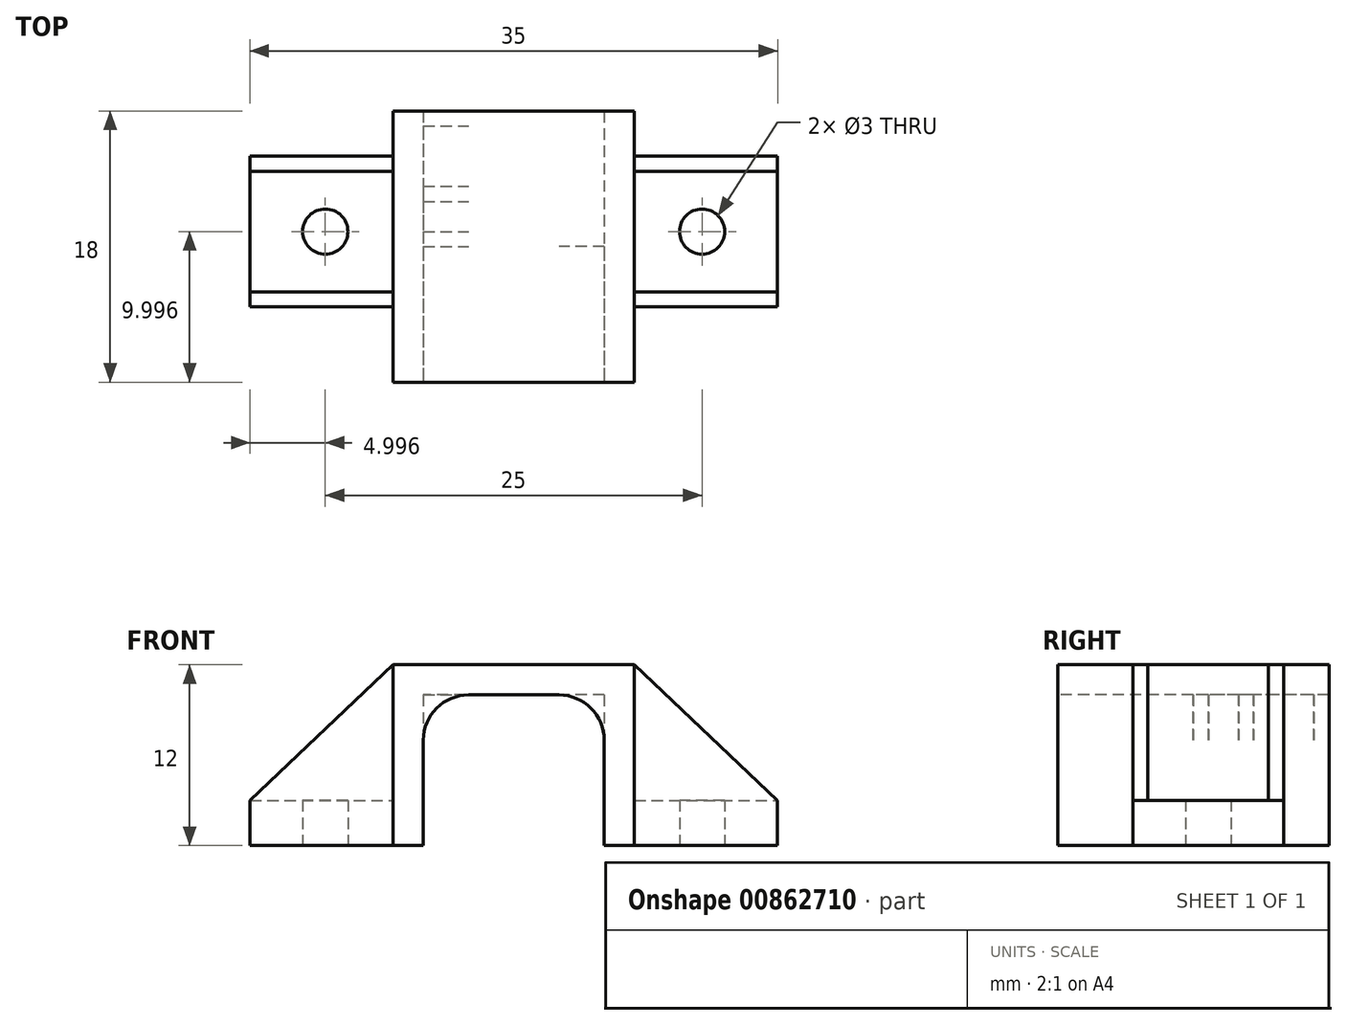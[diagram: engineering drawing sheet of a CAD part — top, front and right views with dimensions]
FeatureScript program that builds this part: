
annotation { "Feature Type Name" : "Feature", "Feature Type Description" : "" }
export const myFeature = defineFeature(function(context is Context, id is Id, definition is map)
    precondition{}
    {
        {
            var Q0;
            Q0=qCreatedBy(makeId("Top.planeOp"),FACE);
            var sketch = newSketch(context, id + "F0", { "sketchPlane" : qUnion([Q0])});
            skLineSegment(sketch, "E0.bottom", {"start": v(-19.82, -6.68) * mm, "end": v(15.18, -6.68) * mm});
            skLineSegment(sketch, "E0.top", {"start": v(-19.82, 3.32) * mm, "end": v(15.18, 3.32) * mm});
            skLineSegment(sketch, "E0.left", {"start": v(-19.82, -6.68) * mm, "end": v(-19.82, 3.32) * mm});
            skLineSegment(sketch, "E0.right", {"start": v(15.18, -6.68) * mm, "end": v(15.18, 3.32) * mm});
            skCircle(sketch, "E1", {"center": v(-14.82, -1.68) * mm, "radius": 1.5 * mm});
            skCircle(sketch, "E2", {"center": v(10.18, -1.68) * mm, "radius": 1.5 * mm});
            skLineSegment(sketch, "E3.bottom", {"start": v(-10.32, 6.32) * mm, "end": v(5.68, 6.32) * mm});
            skLineSegment(sketch, "E3.top", {"start": v(-10.32, -11.68) * mm, "end": v(5.68, -11.68) * mm});
            skLineSegment(sketch, "E3.left", {"start": v(-10.32, 6.32) * mm, "end": v(-10.32, -11.68) * mm});
            skLineSegment(sketch, "E3.right", {"start": v(5.68, 6.32) * mm, "end": v(5.68, -11.68) * mm});
            skSolve(sketch);
        }
        {
            var Q0;
            {var subQ5=sQuery(id+"F0.wireOp",EDGE,"E3.bottom");Q0=makeQuery(id+"F0.imprint","IMPRINT",FACE,{"disambiguationData":[TD([[makeQuery(id+"F0.imprint","IMPRINT",EDGE,{"derivedFrom":subQ5}),-1.0]])]});}
            var Q1;
            {var subQ0=sQuery(id+"F0.wireOp",EDGE,"E3.left");var subQ1=sQuery(id+"F0.wireOp",EDGE,"E0.bottom");var subQ2=makeQuery(id+"F0.imprint","INTERSECT",VERTEX,{"derivedFrom":[subQ1,subQ0]});Q1=makeQuery(id+"F0.imprint","IMPRINT",FACE,{"disambiguationData":[TD([[makeQuery(id+"F0.imprint","IMPRINT",EDGE,{"disambiguationData":[TD([[subQ2,-1.0]])],"derivedFrom":subQ1}),1.0]])]});}
            var Q2;
            {var subQ0=sQuery(id+"F0.wireOp",EDGE,"E0.left");Q2=makeQuery(id+"F0.imprint","IMPRINT",FACE,{"disambiguationData":[TD([[makeQuery(id+"F0.imprint","IMPRINT",EDGE,{"derivedFrom":subQ0}),-1.0]])]});}
            var Q3;
            {var subQ5=sQuery(id+"F0.wireOp",EDGE,"E3.top");Q3=makeQuery(id+"F0.imprint","IMPRINT",FACE,{"disambiguationData":[TD([[makeQuery(id+"F0.imprint","IMPRINT",EDGE,{"derivedFrom":subQ5}),1.0]])]});}
            var Q4;
            {var subQ0=sQuery(id+"F0.wireOp",EDGE,"E0.right");Q4=makeQuery(id+"F0.imprint","IMPRINT",FACE,{"disambiguationData":[TD([[makeQuery(id+"F0.imprint","IMPRINT",EDGE,{"derivedFrom":subQ0}),1.0]])]});}
            extrude(context, id + "F1", {"entities" : qUnion([Q0, Q1, Q2, Q3, Q4]), "depth" : 3 * mm, "offsetDistance" : 25 * mm});
        }
        {
            var Q0;
            Q0=makeQuery(id+"F1.opExtrude","CAP_FACE",FACE,{"disambiguationData":[OSD([sQuery(id+"F0.wireOp",EDGE,"E0.bottom"),sQuery(id+"F0.wireOp",EDGE,"E0.top"),sQuery(id+"F0.wireOp",EDGE,"E0.left"),sQuery(id+"F0.wireOp",EDGE,"E0.right"),sQuery(id+"F0.wireOp",EDGE,"E1"),sQuery(id+"F0.wireOp",EDGE,"E2"),sQuery(id+"F0.wireOp",EDGE,"E3.bottom"),sQuery(id+"F0.wireOp",EDGE,"E3.top"),sQuery(id+"F0.wireOp",EDGE,"E3.left"),sQuery(id+"F0.wireOp",EDGE,"E3.right")])],"isStart":false});
            var sketch = newSketch(context, id + "F2", { "sketchPlane" : qUnion([Q0])});
            skLineSegment(sketch, "E4.bottom", {"start": v(-10.32, -11.68) * mm, "end": v(5.68, -11.68) * mm});
            skLineSegment(sketch, "E4.top", {"start": v(-10.32, 6.32) * mm, "end": v(5.68, 6.32) * mm});
            skLineSegment(sketch, "E4.left", {"start": v(-10.32, -11.68) * mm, "end": v(-10.32, 6.32) * mm});
            skLineSegment(sketch, "E4.right", {"start": v(5.68, -11.68) * mm, "end": v(5.68, 6.32) * mm});
            skSolve(sketch);
        }
        {
            var Q0;
            {var subQ8=sQuery(id+"F2.wireOp",EDGE,"E4.bottom");Q0=makeQuery(id+"F2.imprint","IMPRINT",FACE,{"disambiguationData":[TD([[makeQuery(id+"F2.imprint","IMPRINT",EDGE,{"derivedFrom":subQ8}),1.0]])]});}
            extrude(context, id + "F3", {"entities" : qUnion([Q0]), "operationType" : NewBodyOperationType.ADD, "depth" : 9 * mm, "offsetDistance" : 25 * mm});
        }
        {
            var Q0;
            Q0=makeQuery(id+"F3.boolean.opBoolean","MERGE",FACE,{"derivedFrom":[makeQuery(id+"F1.opExtrude","SWEPT_FACE",FACE,{"disambiguationData":[OSD([sQuery(id+"F0.wireOp",EDGE,"E3.top")])]}),makeQuery(id+"F3.opExtrude","SWEPT_FACE",FACE,{"disambiguationData":[OSD([sQuery(id+"F2.wireOp",EDGE,"E4.bottom")])]})]});
            var sketch = newSketch(context, id + "F4", { "sketchPlane" : qUnion([Q0])});
            skLineSegment(sketch, "E5.bottom", {"start": v(-8.32, 0) * mm, "end": v(3.68, 0) * mm});
            skLineSegment(sketch, "E5.top", {"start": v(-8.32, 10) * mm, "end": v(3.68, 10) * mm});
            skLineSegment(sketch, "E5.left", {"start": v(-8.32, 0) * mm, "end": v(-8.32, 10) * mm});
            skLineSegment(sketch, "E5.right", {"start": v(3.68, 0) * mm, "end": v(3.68, 10) * mm});
            skCircle(sketch, "E6", {"center": v(-5.32, 7) * mm, "radius": 3 * mm});
            skCircle(sketch, "E7", {"center": v(0.68, 7) * mm, "radius": 3 * mm});
            skSolve(sketch);
        }
        {
            var Q0;
            {var subQ0=sQuery(id+"F4.wireOp",EDGE,"E6");var subQ1=makeQuery(id+"F4.imprint","INTERSECT",VERTEX,{"derivedFrom":[sQuery(id+"F4.wireOp",EDGE,"E5.top"),subQ0]});Q0=makeQuery(id+"F4.imprint","IMPRINT",FACE,{"disambiguationData":[TD([[makeQuery(id+"F4.imprint","IMPRINT",EDGE,{"disambiguationData":[TD([[subQ1,1.0]])],"derivedFrom":subQ0}),1.0]])]});}
            var Q1;
            {var subQ0=sQuery(id+"F4.wireOp",EDGE,"E6");var subQ1=sQuery(id+"F4.wireOp",EDGE,"E5.top");var subQ2=makeQuery(id+"F4.imprint","INTERSECT",VERTEX,{"derivedFrom":[subQ1,subQ0]});Q1=makeQuery(id+"F4.imprint","IMPRINT",FACE,{"disambiguationData":[TD([[makeQuery(id+"F4.imprint","IMPRINT",EDGE,{"disambiguationData":[TD([[subQ2,-1.0]])],"derivedFrom":subQ1}),-1.0]])]});}
            var Q2;
            {var subQ0=sQuery(id+"F4.wireOp",EDGE,"E7");var subQ1=makeQuery(id+"F4.imprint","INTERSECT",VERTEX,{"derivedFrom":[sQuery(id+"F4.wireOp",EDGE,"E5.top"),subQ0]});Q2=makeQuery(id+"F4.imprint","IMPRINT",FACE,{"disambiguationData":[TD([[makeQuery(id+"F4.imprint","IMPRINT",EDGE,{"disambiguationData":[TD([[subQ1,1.0]])],"derivedFrom":subQ0}),1.0]])]});}
            var Q3;
            {var subQ1=sQuery(id+"F4.wireOp",EDGE,"E5.bottom");Q3=makeQuery(id+"F4.imprint","IMPRINT",FACE,{"disambiguationData":[TD([[makeQuery(id+"F4.imprint","IMPRINT",EDGE,{"derivedFrom":subQ1}),1.0]])]});}
            extrude(context, id + "F5", {"entities" : qUnion([Q0, Q1, Q2, Q3]), "operationType" : NewBodyOperationType.REMOVE, "endBound" : BoundingType.THROUGH_ALL, "oppositeDirection" : true, "depth" : 25 * mm, "offsetDistance" : 25 * mm});
        }
        {
            var Q0;
            {var subQ0=sQuery(id+"F0.wireOp",EDGE,"E0.bottom");Q0=makeQuery(id+"F1.opExtrude","SWEPT_FACE",FACE,{"disambiguationData":[OSD([subQ0]),TDD([makeQuery(id+"F0.imprint","IMPRINT",EDGE,{"disambiguationData":[TD([[makeQuery(id+"F0.imprint","INTERSECT",VERTEX,{"derivedFrom":[subQ0,sQuery(id+"F0.wireOp",EDGE,"E0.left")]}),-1.0]])],"derivedFrom":subQ0})])]});}
            var sketch = newSketch(context, id + "F6", { "sketchPlane" : qUnion([Q0])});
            skLineSegment(sketch, "E8", {"start": v(-19.82, 3) * mm, "end": v(-10.32, 12) * mm});
            skLineSegment(sketch, "E9", {"start": v(-10.32, 12) * mm, "end": v(-10.32, 3) * mm});
            skLineSegment(sketch, "E10", {"start": v(-10.32, 3) * mm, "end": v(-19.82, 3) * mm});
            skSolve(sketch);
        }
        {
            var Q0;
            Q0=makeQuery(id+"F6.imprint","IMPRINT",FACE,{"disambiguationData":[TD([[makeQuery(id+"F6.imprint","IMPRINT",EDGE,{"derivedFrom":sQuery(id+"F6.wireOp",EDGE,"E8")}),-1.0]])]});
            extrude(context, id + "F7", {"entities" : qUnion([Q0]), "operationType" : NewBodyOperationType.ADD, "oppositeDirection" : true, "depth" : 1 * mm, "offsetDistance" : 25 * mm});
        }
        {
            var Q0;
            {var subQ0=sQuery(id+"F0.wireOp",EDGE,"E0.top");Q0=makeQuery(id+"F1.opExtrude","SWEPT_FACE",FACE,{"disambiguationData":[OSD([subQ0]),TDD([makeQuery(id+"F0.imprint","IMPRINT",EDGE,{"disambiguationData":[TD([[makeQuery(id+"F0.imprint","INTERSECT",VERTEX,{"derivedFrom":[subQ0,sQuery(id+"F0.wireOp",EDGE,"E0.left")]}),-1.0]])],"derivedFrom":subQ0})])]});}
            var sketch = newSketch(context, id + "F8", { "sketchPlane" : qUnion([Q0])});
            skLineSegment(sketch, "E11", {"start": v(19.82, 3) * mm, "end": v(10.32, 12) * mm});
            skLineSegment(sketch, "E12", {"start": v(10.32, 12) * mm, "end": v(10.32, 3) * mm});
            skLineSegment(sketch, "E13", {"start": v(10.32, 3) * mm, "end": v(19.82, 3) * mm});
            skSolve(sketch);
        }
        {
            var Q0;
            Q0=makeQuery(id+"F8.imprint","IMPRINT",FACE,{"disambiguationData":[TD([[makeQuery(id+"F8.imprint","IMPRINT",EDGE,{"derivedFrom":sQuery(id+"F8.wireOp",EDGE,"E11")}),1.0]])]});
            extrude(context, id + "F9", {"entities" : qUnion([Q0]), "operationType" : NewBodyOperationType.ADD, "oppositeDirection" : true, "depth" : 1 * mm, "offsetDistance" : 25 * mm});
        }
        {
            var Q0;
            {var subQ0=sQuery(id+"F0.wireOp",EDGE,"E0.top");Q0=makeQuery(id+"F1.opExtrude","SWEPT_FACE",FACE,{"disambiguationData":[OSD([subQ0]),TDD([makeQuery(id+"F0.imprint","IMPRINT",EDGE,{"disambiguationData":[TD([[makeQuery(id+"F0.imprint","INTERSECT",VERTEX,{"derivedFrom":[subQ0,sQuery(id+"F0.wireOp",EDGE,"E0.right")]}),1.0]])],"derivedFrom":subQ0})])]});}
            var sketch = newSketch(context, id + "F10", { "sketchPlane" : qUnion([Q0])});
            skLineSegment(sketch, "E14", {"start": v(-15.18, 3) * mm, "end": v(-5.68, 3) * mm});
            skLineSegment(sketch, "E15", {"start": v(-5.68, 3) * mm, "end": v(-5.68, 12) * mm});
            skLineSegment(sketch, "E16", {"start": v(-5.68, 12) * mm, "end": v(-15.18, 3) * mm});
            skSolve(sketch);
        }
        {
            var Q0;
            Q0=makeQuery(id+"F10.imprint","IMPRINT",FACE,{"disambiguationData":[TD([[makeQuery(id+"F10.imprint","IMPRINT",EDGE,{"derivedFrom":sQuery(id+"F10.wireOp",EDGE,"E14")}),-1.0]])]});
            extrude(context, id + "F11", {"entities" : qUnion([Q0]), "operationType" : NewBodyOperationType.ADD, "oppositeDirection" : true, "depth" : 1 * mm, "offsetDistance" : 25 * mm});
        }
        {
            var Q0;
            {var subQ0=sQuery(id+"F0.wireOp",EDGE,"E0.bottom");Q0=makeQuery(id+"F1.opExtrude","SWEPT_FACE",FACE,{"disambiguationData":[OSD([subQ0]),TDD([makeQuery(id+"F0.imprint","IMPRINT",EDGE,{"disambiguationData":[TD([[makeQuery(id+"F0.imprint","INTERSECT",VERTEX,{"derivedFrom":[subQ0,sQuery(id+"F0.wireOp",EDGE,"E0.right")]}),1.0]])],"derivedFrom":subQ0})])]});}
            var sketch = newSketch(context, id + "F12", { "sketchPlane" : qUnion([Q0])});
            skLineSegment(sketch, "E17", {"start": v(15.18, 3) * mm, "end": v(5.68, 3) * mm});
            skLineSegment(sketch, "E18", {"start": v(5.68, 3) * mm, "end": v(5.68, 12) * mm});
            skLineSegment(sketch, "E19", {"start": v(5.68, 12) * mm, "end": v(15.18, 3) * mm});
            skSolve(sketch);
        }
        {
            var Q0;
            Q0=makeQuery(id+"F12.imprint","IMPRINT",FACE,{"disambiguationData":[TD([[makeQuery(id+"F12.imprint","IMPRINT",EDGE,{"derivedFrom":sQuery(id+"F12.wireOp",EDGE,"E17")}),1.0]])]});
            extrude(context, id + "F13", {"entities" : qUnion([Q0]), "operationType" : NewBodyOperationType.ADD, "oppositeDirection" : true, "depth" : 1 * mm, "offsetDistance" : 25 * mm});
        }
        {
            var Q0;
            {var subQ0=sQuery(id+"F0.wireOp",EDGE,"E3.left");var subQ1=sQuery(id+"F0.wireOp",EDGE,"E3.top");var subQ2=sQuery(id+"F0.wireOp",EDGE,"E0.bottom");var subQ4=sQuery(id+"F0.wireOp",EDGE,"E0.left");var subQ5=sQuery(id+"F0.wireOp",EDGE,"E0.top");var subQ7=sQuery(id+"F0.wireOp",EDGE,"E3.bottom");var subQ8=sQuery(id+"F0.wireOp",EDGE,"E1");Q0=makeQuery(id+"F5.boolean.opBoolean","SPLIT",FACE,{"disambiguationData":[TD([makeQuery(id+"F1.opExtrude","SWEPT_FACE",FACE,{"disambiguationData":[OSD([subQ4])]})])],"derivedFrom":makeQuery(id+"F1.opExtrude","CAP_FACE",FACE,{"disambiguationData":[OSD([subQ2,subQ5,subQ4,sQuery(id+"F0.wireOp",EDGE,"E0.right"),subQ8,sQuery(id+"F0.wireOp",EDGE,"E2"),subQ7,subQ1,subQ0,sQuery(id+"F0.wireOp",EDGE,"E3.right")])],"isStart":true})});}
            var sketch = newSketch(context, id + "F14", { "sketchPlane" : qUnion([Q0])});
            skLineSegment(sketch, "E20.bottom", {"start": v(-8.32, -6.32) * mm, "end": v(-5.32, -6.32) * mm});
            skLineSegment(sketch, "E20.top", {"start": v(-8.32, -5.32) * mm, "end": v(-5.32, -5.32) * mm});
            skLineSegment(sketch, "E20.left", {"start": v(-8.32, -6.32) * mm, "end": v(-8.32, -5.32) * mm});
            skLineSegment(sketch, "E20.right", {"start": v(-5.32, -6.32) * mm, "end": v(-5.32, -5.32) * mm});
            skLineSegment(sketch, "E21.bottom", {"start": v(-8.32, -1.32) * mm, "end": v(-5.32, -1.32) * mm});
            skLineSegment(sketch, "E21.top", {"start": v(-8.32, -0.32) * mm, "end": v(-5.32, -0.32) * mm});
            skLineSegment(sketch, "E21.left", {"start": v(-8.32, -1.32) * mm, "end": v(-8.32, -0.32) * mm});
            skLineSegment(sketch, "E21.right", {"start": v(-5.32, -1.32) * mm, "end": v(-5.32, -0.32) * mm});
            skLineSegment(sketch, "E22.bottom", {"start": v(-8.32, 1.68) * mm, "end": v(-5.32, 1.68) * mm});
            skLineSegment(sketch, "E22.top", {"start": v(-8.32, 2.68) * mm, "end": v(-5.32, 2.68) * mm});
            skLineSegment(sketch, "E22.left", {"start": v(-8.32, 1.68) * mm, "end": v(-8.32, 2.68) * mm});
            skLineSegment(sketch, "E22.right", {"start": v(-5.32, 1.68) * mm, "end": v(-5.32, 2.68) * mm});
            skLineSegment(sketch, "E23.bottom", {"start": v(3.68, -6.32) * mm, "end": v(0.68, -6.32) * mm});
            skLineSegment(sketch, "E23.top", {"start": v(3.68, 2.68) * mm, "end": v(0.68, 2.68) * mm});
            skLineSegment(sketch, "E23.left", {"start": v(3.68, -6.32) * mm, "end": v(3.68, 2.68) * mm});
            skLineSegment(sketch, "E23.right", {"start": v(0.68, -6.32) * mm, "end": v(0.68, 2.68) * mm});
            skSolve(sketch);
        }
        {
            var Q0;
            Q0=makeQuery(id+"F14.imprint","IMPRINT",FACE,{"disambiguationData":[TD([[makeQuery(id+"F14.imprint","IMPRINT",EDGE,{"derivedFrom":sQuery(id+"F14.wireOp",EDGE,"E21.bottom")}),1.0]])]});
            var Q1;
            Q1=makeQuery(id+"F14.imprint","IMPRINT",FACE,{"disambiguationData":[TD([[makeQuery(id+"F14.imprint","IMPRINT",EDGE,{"derivedFrom":sQuery(id+"F14.wireOp",EDGE,"E20.bottom")}),1.0]])]});
            var Q2;
            Q2=makeQuery(id+"F14.imprint","IMPRINT",FACE,{"disambiguationData":[TD([[makeQuery(id+"F14.imprint","IMPRINT",EDGE,{"derivedFrom":sQuery(id+"F14.wireOp",EDGE,"E23.bottom")}),-1.0]])]});
            var Q3;
            Q3=makeQuery(id+"F14.imprint","IMPRINT",FACE,{"disambiguationData":[TD([[makeQuery(id+"F14.imprint","IMPRINT",EDGE,{"derivedFrom":sQuery(id+"F14.wireOp",EDGE,"E22.bottom")}),1.0]])]});
            extrude(context, id + "F15", {"entities" : qUnion([Q0, Q1, Q2, Q3]), "operationType" : NewBodyOperationType.REMOVE, "oppositeDirection" : true, "depth" : 10 * mm, "offsetDistance" : 25 * mm});
        }
    });
